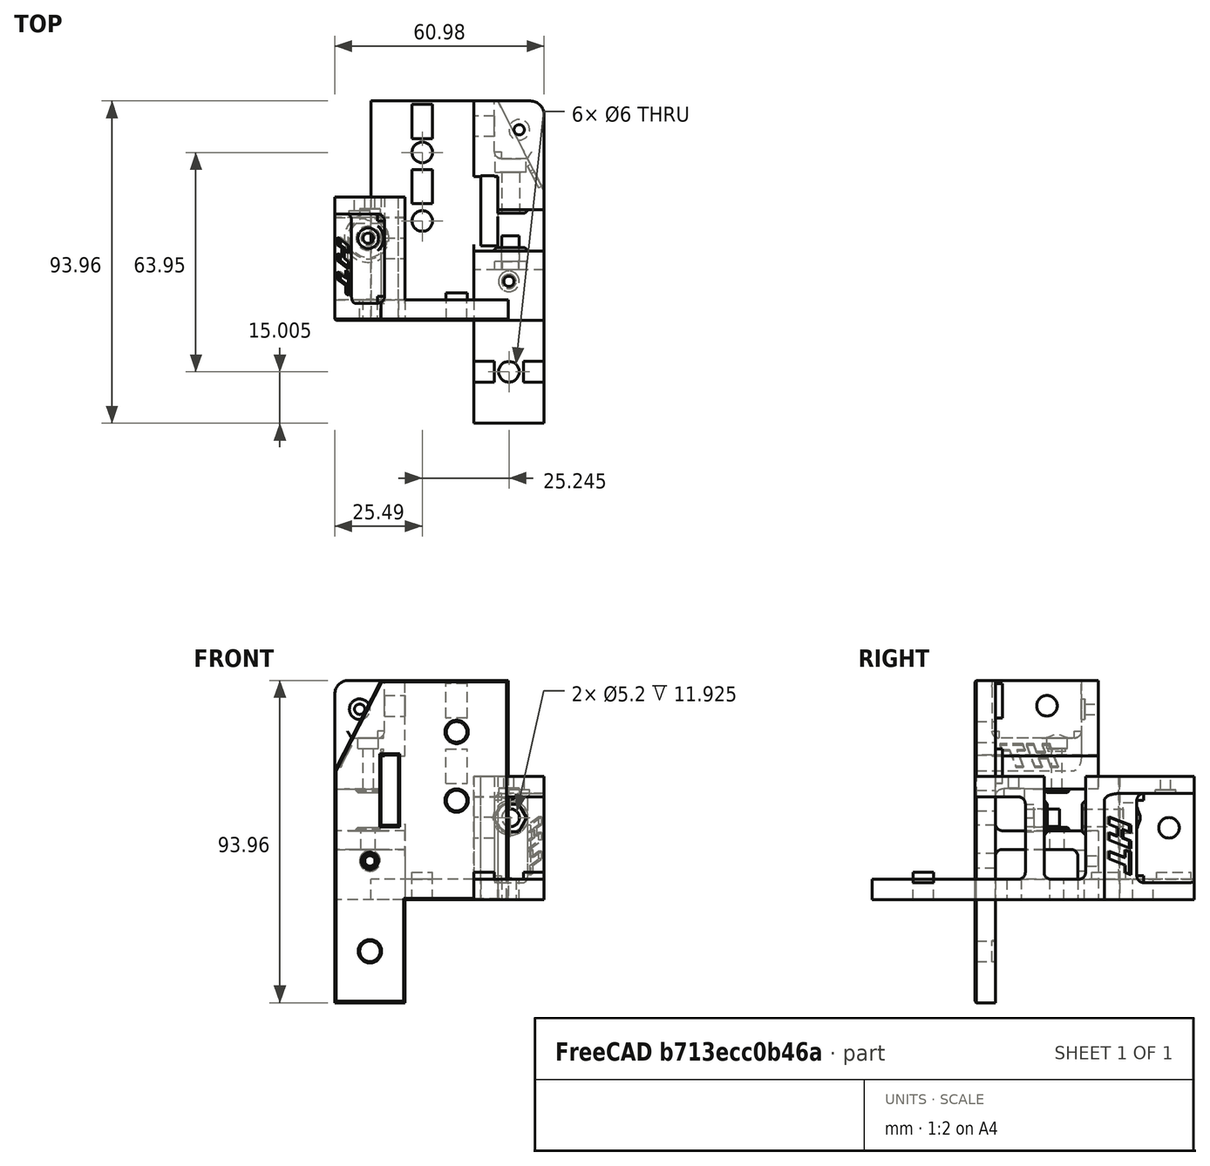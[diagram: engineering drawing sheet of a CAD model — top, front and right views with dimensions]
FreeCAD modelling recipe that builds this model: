
FCSTD DOCUMENT  (FreeCAD 0.18R16146 (Git))
Label: read-idler-left-2
License: All rights reserved
LicenseURL: http://en.wikipedia.org/wiki/All_rights_reserved
objects: Part::Cylinder×14, Part::Box×10, Part::Cut×10, Part::MultiFuse×7, Part::Feature×4, Part::Chamfer×4
note: 49 computed .brp shape members not serialized (recipe doc carries the construction recipe); baked Part::Feature solids carry a one-line shape summary decoded from their .brp

FEATURE [Part::Feature] Part__Feature069  label="PulleyMount_REAR_LEFT_Body"
  Placement = pos=(432.5,-458.82,6) rot=(0,1,0;1.5708rad)
  shape: bbox 52.27 x 93.95 x 36 mm, 93 faces (baked)
FEATURE [Part::Box] Box  label="Cube"
  AttacherType = Attacher::AttachEngine3D
  Height = 3
  Length = 6
  Placement = pos=(-8,53,5) rot=(0,0,1;0rad)
  Width = 10
FEATURE [Part::Feature] Part__Feature069001  label="PulleyMount_REAR_LEFT_Body001"
  shape: bbox 52.27 x 93.95 x 36 mm, 93 faces (baked)
FEATURE [Part::Box] Box001  label="Cube001"
  AttacherType = Attacher::AttachEngine3D
  Height = 3
  Length = 6
  Placement = pos=(-8,34,5) rot=(0,0,1;0rad)
  Width = 10
FEATURE [Part::Box] Box002  label="Cube002"
  AttacherType = Attacher::AttachEngine3D
  Height = 3
  Length = 6
  Placement = pos=(10,-17.99,5) rot=(0,0,1;0rad)
  Width = 6
FEATURE [Part::Box] Box003  label="Cube003"
  AttacherType = Attacher::AttachEngine3D
  Height = 3
  Length = 6
  Placement = pos=(24.49,-17.99,5) rot=(0,0,1;0rad)
  Width = 6
FEATURE [Part::MultiFuse] Fusion
  Shapes = -> [Box003,Box002,Box001,Part__Feature069001,Box]
FEATURE [Part::Feature] Fusion001
  shape: bbox 52.27 x 93.95 x 36 mm, 113 faces (baked)
FEATURE [Part::Chamfer] Chamfer
  Base = -> Fusion001
  Edges = 15 edges r=0.4: [Edge55,Edge69,Edge86,Edge89,Edge91,Edge101,Edge106,Edge119,Edge129,Edge139,Edge155,Edge180,Edge181,Edge182,Edge183]
FEATURE [Part::Cylinder] Cylinder  label="pos"
  Angle = 360
  AttacherType = Attacher::AttachEngine3D
  Height = 10
  Placement = pos=(20.74,14.7,23.92) rot=(-1,0,0;1.5708rad)
  Radius = 2.55
FEATURE [Part::Cylinder] Cylinder001  label="pos001"
  Angle = 360
  AttacherType = Attacher::AttachEngine3D
  Height = 5.45
  Placement = pos=(20.74,14.7,23.92) rot=(-1,0,0;1.5708rad)
  Radius = 5.55
FEATURE [Part::Cylinder] Cylinder002  label="pos002"
  Angle = 360
  AttacherType = Attacher::AttachEngine3D
  Height = 14.92
  Placement = pos=(20.74,32.26,23.92) rot=(-1,0,0;1.5708rad)
  Radius = 5.55
FEATURE [Part::Chamfer] Chamfer001
  Base = -> Cylinder002
  Edges = 1 edges: [Edge1 r1=2 r2=1]
FEATURE [Part::MultiFuse] Fusion002
  Shapes = -> [Chamfer,Cylinder001]
FEATURE [Part::Feature] Body001
  Placement = pos=(20.74,14.7,23.92) rot=(-1,0,0;1.5708rad)
  shape: bbox 5.543 x 3 x 6.4 mm, 8 faces (baked)
FEATURE [Part::Cylinder] Cylinder004  label="pos003"
  Angle = 360
  AttacherType = Attacher::AttachEngine3D
  Height = 37
  Placement = pos=(20.74,14.7,23.92) rot=(-1,0,0;1.5708rad)
  Radius = 1.5
FEATURE [Part::Cylinder] Cylinder005  label="pos004"
  Angle = 360
  AttacherType = Attacher::AttachEngine3D
  Height = 3
  Placement = pos=(20.74,44.18,23.92) rot=(-1,0,0;1.5708rad)
  Radius = 3
FEATURE [Part::Cylinder] Cylinder006  label="pos005"
  Angle = 360
  AttacherType = Attacher::AttachEngine3D
  Height = 5
  Placement = pos=(20.74,27.26,23.92) rot=(-1,0,0;1.5708rad)
  Radius = 7
FEATURE [Part::Cylinder] Cylinder007  label="pos006"
  Angle = 360
  AttacherType = Attacher::AttachEngine3D
  Height = 5
  Placement = pos=(20.74,20.15,23.92) rot=(-1,0,0;1.5708rad)
  Radius = 6
FEATURE [Part::Box] Box004  label="Cube004"
  AttacherType = Attacher::AttachEngine3D
  Height = 24
  Length = 10
  Placement = pos=(7,25,12) rot=(0,0,1;0rad)
  Width = 19
FEATURE [Part::Cut] Cut
  Base = -> Chamfer001
  Tool = -> Box004
FEATURE [Part::MultiFuse] Fusion003
  Shapes = -> [Cylinder005,Fusion002,Cut]
FEATURE [Part::Cut] Cut001
  Base = -> Fusion003
  Tool = -> Body001
FEATURE [Part::Cut] Cut002
  Base = -> Cut001
  Tool = -> Cylinder004
FEATURE [Part::Cut] Cut003
  Base = -> Cut002
  Tool = -> Cylinder007
FEATURE [Part::Cylinder] Cylinder008  label="pos007"
  Angle = 360
  AttacherType = Attacher::AttachEngine3D
  Height = 1.05
  Placement = pos=(20.74,20.15,23.92) rot=(-1,0,0;1.5708rad)
  Radius = 3.5
FEATURE [Part::Cylinder] Cylinder009  label="pos008"
  Angle = 360
  AttacherType = Attacher::AttachEngine3D
  Height = 1.05
  Placement = pos=(20.74,31.21,23.92) rot=(-1,0,0;1.5708rad)
  Radius = 3.5
FEATURE [Part::Cylinder] Cylinder010  label="pos009"
  Angle = 360
  AttacherType = Attacher::AttachEngine3D
  Height = 1.05
  Placement = pos=(20.74,20.15,23.92) rot=(-1,0,0;1.5708rad)
  Radius = 1.5
FEATURE [Part::Cylinder] Cylinder011  label="pos010"
  Angle = 360
  AttacherType = Attacher::AttachEngine3D
  Height = 1.05
  Placement = pos=(20.74,31.21,23.92) rot=(-1,0,0;1.5708rad)
  Radius = 1.5
FEATURE [Part::Cut] Cut005
  Base = -> Cylinder009
  Tool = -> Cylinder011
FEATURE [Part::Cut] Cut006
  Base = -> Cylinder008
  Tool = -> Cylinder010
FEATURE [Part::Chamfer] Chamfer002
  Base = -> Cut005
  Edges = 1 edges r=0.5: [Edge3]
  Placement = pos=(0,0.1,0) rot=(0,0,1;0rad)
FEATURE [Part::Chamfer] Chamfer003
  Base = -> Cut006
  Edges = 1 edges r=0.5: [Edge1]
  Placement = pos=(0,-0.09,0) rot=(0,0,1;0rad)
FEATURE [Part::Cylinder] Cylinder012  label="pos011"
  Angle = 360
  AttacherType = Attacher::AttachEngine3D
  Height = 3
  Placement = pos=(20.74,44.18,23.92) rot=(-1,0,0;1.5708rad)
  Radius = 3
FEATURE [Part::Cut] Cut004
  Base = -> Cut003
  Tool = -> Cylinder006
FEATURE [Part::Cut] Cut007
  Base = -> Cut004
  Tool = -> Cylinder012
FEATURE [Part::MultiFuse] Fusion004
  Shapes = -> [Cut007,Chamfer003,Chamfer002]
FEATURE [Part::Box] Box005  label="Cube005"
  AttacherType = Attacher::AttachEngine3D
  Height = 3
  Length = 6
  Placement = pos=(24.49,-18.09,5) rot=(0,0,1;0rad)
  Width = 6.2
FEATURE [Part::Box] Box006  label="Cube006"
  AttacherType = Attacher::AttachEngine3D
  Height = 3
  Length = 6
  Placement = pos=(10,-18.09,5) rot=(0,0,1;0rad)
  Width = 6.2
FEATURE [Part::Box] Box007  label="Cube007"
  AttacherType = Attacher::AttachEngine3D
  Height = 3
  Length = 6.2
  Placement = pos=(-8.1,34.01,5) rot=(0,0,1;0rad)
  Width = 10
FEATURE [Part::Box] Box008  label="Cube008"
  AttacherType = Attacher::AttachEngine3D
  Height = 3
  Length = 6.2
  Placement = pos=(-8.1,53,5) rot=(0,0,1;0rad)
  Width = 10
FEATURE [Part::MultiFuse] Fusion005
  Shapes = -> [Box008,Box007,Box006,Box005]
FEATURE [Part::MultiFuse] Fusion006
  Shapes = -> [Fusion005,Fusion004]
FEATURE [Part::Cylinder] Cylinder013  label="pos012"
  Angle = 360
  AttacherType = Attacher::AttachEngine3D
  Height = 5.45
  Placement = pos=(20.74,14.7,23.92) rot=(-1,0,0;1.5708rad)
  Radius = 3.5
FEATURE [Part::Cylinder] Cylinder014  label="pos013"
  Angle = 360
  AttacherType = Attacher::AttachEngine3D
  Height = 5.45
  Placement = pos=(20.74,14.7,23.92) rot=(-1,0,0;1.5708rad)
  Radius = 2.1
FEATURE [Part::MultiFuse] Fusion007
  Shapes = -> [Fusion006,Cylinder013]
FEATURE [Part::Cut] Cut008
  Base = -> Fusion007
  Placement = pos=(0,0,0) rot=(0,0.707107,0.707107;3.14159rad)
  Tool = -> Cylinder014
FEATURE [Part::Box] Box009  label="Cube009"
  AttacherType = Attacher::AttachEngine3D
  Height = 10
  Length = 32
  Placement = pos=(-38,6,-19) rot=(0,0,1;0rad)
  Width = 10
FEATURE [Part::Cut] Cut009
  Base = -> Cut008
  Tool = -> Box009
